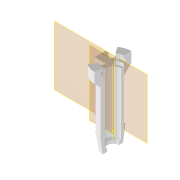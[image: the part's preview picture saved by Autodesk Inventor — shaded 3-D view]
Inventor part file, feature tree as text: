
AUTODESK INVENTOR PART (.ipt)
format: ipt  version: 2022 (Build 260153000, 153)  size: 266,240 bytes
history: native  units: mm
features: sketch x7, extrude x5, other x5, projected_geometry x3, plane x2, revolve x2, mirror x1, reference x1
ambient origin geometry x8: Origin, YZ Plane, XZ Plane, XY Plane, X Axis, Y Axis, Z Axis, Center Point
bodies: Volumenkörper1 (feature_tree)
feature tree (26):
  plane  "Arbeitsebene1"
  extrude  "Extrusion1"  Depth=3.0mm
  extrude  "Extrusion2"  Depth=34.0mm
  extrude  "Extrusion3"  Depth=6.0mm
  extrude  "Extrusion4"  Depth=6.0mm
  extrude  "Extrusion5"  Depth=6.0mm
  other  "Arbeitsachse1"
  revolve  "Umdrehung1"
  plane  "Arbeitsebene2"
  mirror  "Spiegeln2"
  revolve  "Umdrehung2"
  sketch  "Skizze1"  dims[d0=6.0mm d1=3.0mm]
  sketch  "Skizze2"  dims[d2=6.0mm d3=34.0mm]
  reference  "Referenz1"
  sketch  "Skizze3"  dims[d4=8.0mm d5=6.0mm]
  projected_geometry  "Projizierte Kontur1"
  sketch  "Skizze4"  dims[d6=6.0mm d7=6.0mm]
  projected_geometry  "Projizierte Kontur2"
  sketch  "Skizze5"  dims[d8=6.0mm d9=6.0mm]
  sketch  "Skizze6"  dims[d10=6.0mm]
  projected_geometry  "Projizierte Kontur3"
  other  "Arbeitspunkt1"
  sketch  "Skizze7"  dims[d11=6.1mm d12=6.1mm d13=6.0mm d14=6.0mm d15=0.0mm d16=4.0mm d17=90.0deg d18=15.0deg d19=15.0deg d20=6.0mm d21=0.0mm d22=6.0mm d23=3.93mm d24=0.0mm d25=12.0mm d26=0.0mm d27=14.65mm d28=10.0mm d29=4.0mm d30=10.0mm d31=0.0mm d32=0.0mm d33=0.0mm d36=9.5mm d37=9.5mm d38=3.0mm d39=45.0deg d40=3.0mm d41=11.25mm d42=16.75mm d43=3.0mm d44=6.108652mm d45=14.0mm d47=5.25mm d48=180.0deg]
  other  "<userpath>\Documents\GitHub\VolterVOneHACKS\INVENTOR\VolteraOne_tool.ipj.iam"
  other  "VolteraOne_tool.ipj.iam"
  other  "00_rod_6mm:1"
